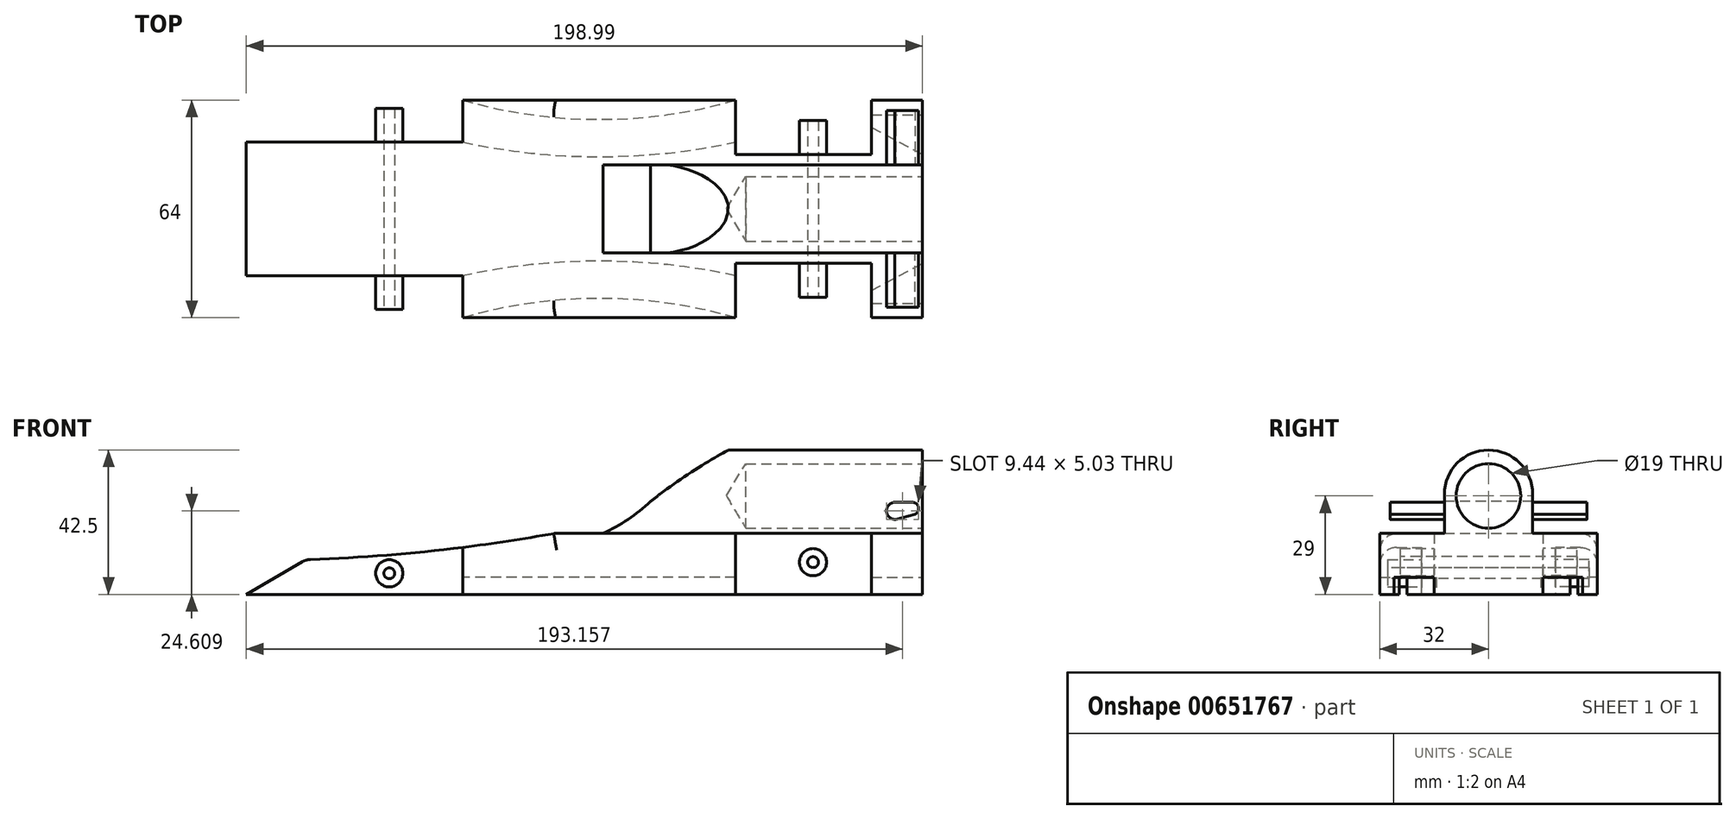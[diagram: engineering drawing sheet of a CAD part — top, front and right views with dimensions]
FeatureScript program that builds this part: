
annotation { "Feature Type Name" : "Feature", "Feature Type Description" : "" }
export const myFeature = defineFeature(function(context is Context, id is Id, definition is map)
    precondition{}
    {
        {
            var Q0;
            Q0=qCreatedBy(makeId("Front.planeOp"),FACE);
            var sketch = newSketch(context, id + "F0", { "sketchPlane" : qUnion([Q0])});
            skLineSegment(sketch, "E0", {"start": v(-86.8, 0) * mm, "end": v(113.2, 0) * mm});
            skLineSegment(sketch, "E1", {"start": v(113.2, 0) * mm, "end": v(113.2, 18) * mm});
            skLineSegment(sketch, "E2", {"start": v(-86.8, 0) * mm, "end": v(-86.8, 10) * mm});
            skLineSegment(sketch, "E3", {"start": v(113.2, 18) * mm, "end": v(5.13, 18) * mm});
            skArc(sketch, "E4", {"start": v(-86.8, 10) * mm, "mid": v(-40.65, 11.89) * mm, "end": v(5.13, 18) * mm});
            skSolve(sketch);
        }
        {
            var Q0;
            Q0=makeQuery(id+"F0.imprint","IMPRINT",FACE,{"disambiguationData":[TD([[makeQuery(id+"F0.imprint","IMPRINT",EDGE,{"derivedFrom":sQuery(id+"F0.wireOp",EDGE,"E0")}),1.0]])]});
            extrude(context, id + "F1", {"entities" : qUnion([Q0]), "oppositeDirection" : true, "depth" : 32 * mm, "offsetDistance" : 25 * mm});
        }
        {
            var Q0;
            Q0=makeQuery(id+"F1.opExtrude","SWEPT_FACE",FACE,{"disambiguationData":[OSD([sQuery(id+"F0.wireOp",EDGE,"E0")])]});
            var sketch = newSketch(context, id + "F2", { "sketchPlane" : qUnion([Q0])});
            skLineSegment(sketch, "E5", {"start": v(-22.02, -32) * mm, "end": v(-22.02, -19.65) * mm});
            skLineSegment(sketch, "E6", {"start": v(-22.02, -19.65) * mm, "end": v(-86.8, -19.65) * mm});
            skSolve(sketch);
        }
        {
            var Q0;
            Q0 = qSketchRegion(id + "F2", true);
            var Q1;
            {var subQ0=sQuery(id+"F2.wireOp",EDGE,"E5");Q1=makeQuery(id+"F2.imprint","IMPRINT",FACE,{"disambiguationData":[TD([[makeQuery(id+"F2.imprint","IMPRINT",EDGE,{"derivedFrom":subQ0}),1.0]])]});}
            extrude(context, id + "F3", {"entities" : qUnion([Q0, Q1]), "operationType" : NewBodyOperationType.REMOVE, "endBound" : BoundingType.THROUGH_ALL, "oppositeDirection" : true, "depth" : 25 * mm, "offsetDistance" : 25 * mm});
        }
        {
            var Q0;
            Q0=makeQuery(id+"F1.opExtrude","SWEPT_FACE",FACE,{"disambiguationData":[OSD([sQuery(id+"F0.wireOp",EDGE,"E0")])]});
            var sketch = newSketch(context, id + "F4", { "sketchPlane" : qUnion([Q0])});
            skLineSegment(sketch, "E7", {"start": v(113.2, -32) * mm, "end": v(98.2, -32) * mm, "construction": true});
            skLineSegment(sketch, "E8.bottom", {"start": v(98.2, -32) * mm, "end": v(58.2, -32) * mm});
            skLineSegment(sketch, "E8.top", {"start": v(98.2, -16) * mm, "end": v(58.2, -16) * mm});
            skLineSegment(sketch, "E8.left", {"start": v(98.2, -32) * mm, "end": v(98.2, -16) * mm});
            skLineSegment(sketch, "E8.right", {"start": v(58.2, -32) * mm, "end": v(58.2, -16) * mm});
            skSolve(sketch);
        }
        {
            var Q0;
            Q0=makeQuery(id+"F4.imprint","IMPRINT",FACE,{"disambiguationData":[TD([[makeQuery(id+"F4.imprint","IMPRINT",EDGE,{"derivedFrom":sQuery(id+"F4.wireOp",EDGE,"E8.bottom")}),1.0]])]});
            extrude(context, id + "F5", {"entities" : qUnion([Q0]), "operationType" : NewBodyOperationType.REMOVE, "endBound" : BoundingType.THROUGH_ALL, "oppositeDirection" : true, "depth" : 25 * mm, "offsetDistance" : 25 * mm});
        }
        {
            var Q0;
            Q0=makeQuery(id+"F1.opExtrude","SWEPT_FACE",FACE,{"disambiguationData":[OSD([sQuery(id+"F0.wireOp",EDGE,"E1")])]});
            var sketch = newSketch(context, id + "F6", { "sketchPlane" : qUnion([Q0])});
            skLineSegment(sketch, "E9", {"start": v(13, 18) * mm, "end": v(13, 29.5) * mm});
            skLineSegment(sketch, "E10", {"start": v(0, 18) * mm, "end": v(0, 42.5) * mm});
            skArc(sketch, "E11", {"start": v(13, 29.5) * mm, "mid": v(9.2, 38.7) * mm, "end": v(0, 42.5) * mm});
            skLineSegment(sketch, "E12", {"start": v(0, 18) * mm, "end": v(13, 18) * mm});
            skSolve(sketch);
        }
        {
            var Q0;
            {var subQ0=sQuery(id+"F6.wireOp",EDGE,"E9");Q0=makeQuery(id+"F6.imprint","IMPRINT",FACE,{"disambiguationData":[TD([[makeQuery(id+"F6.imprint","IMPRINT",EDGE,{"derivedFrom":subQ0}),1.0]])]});}
            extrude(context, id + "F7", {"entities" : qUnion([Q0]), "operationType" : NewBodyOperationType.ADD, "oppositeDirection" : true, "depth" : 80 * mm, "offsetDistance" : 25 * mm});
        }
        {
            var Q0;
            Q0=makeQuery(id+"F7.boolean.opBoolean","MERGE",FACE,{"derivedFrom":[makeQuery(id+"F1.opExtrude","CAP_FACE",FACE,{"disambiguationData":[OSD([sQuery(id+"F0.wireOp",EDGE,"E0"),sQuery(id+"F0.wireOp",EDGE,"E1"),sQuery(id+"F0.wireOp",EDGE,"E2"),sQuery(id+"F0.wireOp",EDGE,"E3"),sQuery(id+"F0.wireOp",EDGE,"E4")])],"isStart":true}),makeQuery(id+"F7.opExtrude","SWEPT_FACE",FACE,{"disambiguationData":[OSD([sQuery(id+"F6.wireOp",EDGE,"E10")])]})]});
            var sketch = newSketch(context, id + "F8", { "sketchPlane" : qUnion([Q0])});
            skArc(sketch, "E13", {"start": v(19.17, 18) * mm, "mid": v(33.82, 27.98) * mm, "end": v(44, 42.5) * mm});
            skSolve(sketch);
        }
        {
            var Q0;
            {var subQ0=sQuery(id+"F8.wireOp",EDGE,"E13");var subQ1=makeQuery(id+"F1.opExtrude","CAP_EDGE",EDGE,{"disambiguationData":[OSD([sQuery(id+"F0.wireOp",EDGE,"E3")])],"isStart":true});var subQ2=makeQuery(id+"F8.imprint","INTERSECT",VERTEX,{"derivedFrom":[subQ1,subQ0]});Q0=makeQuery(id+"F8.imprint","IMPRINT",FACE,{"disambiguationData":[TD([[makeQuery(id+"F8.imprint","IMPRINT",EDGE,{"disambiguationData":[TD([[subQ2,-1.0]])],"derivedFrom":subQ0}),-1.0]])]});}
            extrude(context, id + "F9", {"entities" : qUnion([Q0]), "operationType" : NewBodyOperationType.ADD, "oppositeDirection" : true, "depth" : 13 * mm, "offsetDistance" : 25 * mm});
        }
        {
            var Q0;
            {var subQ0=sQuery(id+"F6.wireOp",EDGE,"E10");var subQ1=sQuery(id+"F0.wireOp",EDGE,"E3");Q0=makeQuery(id+"F9.boolean.opBoolean","MERGE",FACE,{"derivedFrom":[makeQuery(id+"F7.boolean.opBoolean","MERGE",FACE,{"derivedFrom":[makeQuery(id+"F1.opExtrude","CAP_FACE",FACE,{"disambiguationData":[OSD([sQuery(id+"F0.wireOp",EDGE,"E0"),sQuery(id+"F0.wireOp",EDGE,"E1"),sQuery(id+"F0.wireOp",EDGE,"E2"),subQ1,sQuery(id+"F0.wireOp",EDGE,"E4")])],"isStart":true}),makeQuery(id+"F7.opExtrude","SWEPT_FACE",FACE,{"disambiguationData":[OSD([subQ0])]})]}),makeQuery(id+"F9.opExtrude","CAP_FACE",FACE,{"disambiguationData":[OSD([subQ1,subQ0,sQuery(id+"F8.wireOp",EDGE,"E13")])],"isStart":true})]});}
            var sketch = newSketch(context, id + "F10", { "sketchPlane" : qUnion([Q0])});
            skArc(sketch, "E14", {"start": v(56.09, 42.5) * mm, "mid": v(44.33, 35.42) * mm, "end": v(33.2, 27.39) * mm});
            skSolve(sketch);
        }
        {
            var Q0;
            {var subQ0=sQuery(id+"F10.wireOp",EDGE,"E14");Q0=makeQuery(id+"F10.imprint","IMPRINT",FACE,{"disambiguationData":[TD([[makeQuery(id+"F10.imprint","IMPRINT",EDGE,{"derivedFrom":subQ0}),-1.0]])]});}
            extrude(context, id + "F11", {"entities" : qUnion([Q0]), "operationType" : NewBodyOperationType.REMOVE, "endBound" : BoundingType.THROUGH_ALL, "oppositeDirection" : true, "depth" : 25 * mm, "offsetDistance" : 25 * mm});
        }
        {
            var Q0;
            {var subQ0=sQuery(id+"F0.wireOp",EDGE,"E0");var subQ1=sQuery(id+"F0.wireOp",EDGE,"E2");var subQ2=sQuery(id+"F0.wireOp",EDGE,"E4");Q0=makeQuery(id+"FZ9ZeYwKuadsPbT_1.boolean.opBoolean","SPLIT",FACE,{"disambiguationData":[TD([makeQuery(id+"F1.opExtrude","SWEPT_FACE",FACE,{"disambiguationData":[OSD([subQ1])]})])],"derivedFrom":makeQuery(id+"F1.opExtrude","CAP_FACE",FACE,{"disambiguationData":[OSD([subQ0,sQuery(id+"F0.wireOp",EDGE,"E1"),subQ1,sQuery(id+"F0.wireOp",EDGE,"E3"),subQ2])],"isStart":false})});}
            var sketch = newSketch(context, id + "F12", { "sketchPlane" : qUnion([Q0])});
            skSolve(sketch);
        }
        {
            var Q0;
            Q0=makeQuery(id+"F3.boolean.opBoolean","COPY",FACE,{"derivedFrom":makeQuery(id+"F3.opExtrude","SWEPT_FACE",FACE,{"disambiguationData":[OSD([sQuery(id+"F2.wireOp",EDGE,"E6")])]})});
            var sketch = newSketch(context, id + "F13", { "sketchPlane" : qUnion([Q0])});
            skCircle(sketch, "E15", {"center": v(43.7, 6.23) * mm, "radius": 4 * mm});
            skCircle(sketch, "E16", {"center": v(43.7, 6.23) * mm, "radius": 1.6 * mm});
            skSolve(sketch);
        }
        {
            var Q0;
            Q0=makeQuery(id+"F13.imprint","IMPRINT",FACE,{"disambiguationData":[TD([[makeQuery(id+"F13.imprint","IMPRINT",EDGE,{"derivedFrom":sQuery(id+"F13.wireOp",EDGE,"E15")}),1.0]])]});
            extrude(context, id + "F14", {"entities" : qUnion([Q0]), "operationType" : NewBodyOperationType.ADD, "depth" : 10 * mm, "offsetDistance" : 25 * mm});
        }
        {
            var Q0;
            Q0=makeQuery(id+"F14.boolean.opBoolean","SPLIT",FACE,{"disambiguationData":[TD([makeQuery(id+"F14.opExtrude","SWEPT_FACE",FACE,{"disambiguationData":[OSD([sQuery(id+"F13.wireOp",EDGE,"E16")])]})])],"derivedFrom":makeQuery(id+"F3.boolean.opBoolean","COPY",FACE,{"derivedFrom":makeQuery(id+"F3.opExtrude","SWEPT_FACE",FACE,{"disambiguationData":[OSD([sQuery(id+"F2.wireOp",EDGE,"E6")])]})})});
            extrude(context, id + "F15", {"entities" : qUnion([Q0]), "operationType" : NewBodyOperationType.REMOVE, "endBound" : BoundingType.THROUGH_ALL, "oppositeDirection" : true, "depth" : 25 * mm, "offsetDistance" : 25 * mm});
        }
        {
            var Q0;
            Q0=makeQuery(id+"F5.boolean.opBoolean","COPY",FACE,{"derivedFrom":makeQuery(id+"F5.opExtrude","SWEPT_FACE",FACE,{"disambiguationData":[OSD([sQuery(id+"F4.wireOp",EDGE,"E8.top")])]})});
            var sketch = newSketch(context, id + "F16", { "sketchPlane" : qUnion([Q0])});
            skCircle(sketch, "E17", {"center": v(-81, 9.5) * mm, "radius": 4 * mm});
            skCircle(sketch, "E18", {"center": v(-81, 9.5) * mm, "radius": 1.6 * mm});
            skSolve(sketch);
        }
        {
            var Q0;
            Q0=makeQuery(id+"F16.imprint","IMPRINT",FACE,{"disambiguationData":[TD([[makeQuery(id+"F16.imprint","IMPRINT",EDGE,{"derivedFrom":sQuery(id+"F16.wireOp",EDGE,"E17")}),1.0]])]});
            extrude(context, id + "F17", {"entities" : qUnion([Q0]), "operationType" : NewBodyOperationType.ADD, "depth" : 10 * mm, "offsetDistance" : 25 * mm});
        }
        {
            var Q0;
            Q0=makeQuery(id+"F17.boolean.opBoolean","SPLIT",FACE,{"disambiguationData":[TD([makeQuery(id+"F17.opExtrude","SWEPT_FACE",FACE,{"disambiguationData":[OSD([sQuery(id+"F16.wireOp",EDGE,"E18")])]})])],"derivedFrom":makeQuery(id+"F5.boolean.opBoolean","COPY",FACE,{"derivedFrom":makeQuery(id+"F5.opExtrude","SWEPT_FACE",FACE,{"disambiguationData":[OSD([sQuery(id+"F4.wireOp",EDGE,"E8.top")])]})})});
            extrude(context, id + "F18", {"entities" : qUnion([Q0]), "operationType" : NewBodyOperationType.REMOVE, "endBound" : BoundingType.THROUGH_ALL, "oppositeDirection" : true, "depth" : 25 * mm, "offsetDistance" : 25 * mm});
        }
        {
            var Q0;
            {var subQ0=sQuery(id+"F6.wireOp",EDGE,"E9");Q0=makeQuery(id+"F0brN90eAgxFyRM_1.boolean.opBoolean","MERGE",FACE,{"derivedFrom":[makeQuery(id+"F7.boolean.opBoolean","MERGE",FACE,{"derivedFrom":[makeQuery(id+"F1.opExtrude","SWEPT_FACE",FACE,{"disambiguationData":[OSD([sQuery(id+"F0.wireOp",EDGE,"E1")])]}),makeQuery(id+"F7.opExtrude","CAP_FACE",FACE,{"disambiguationData":[OSD([subQ0,sQuery(id+"F6.wireOp",EDGE,"E10"),sQuery(id+"F6.wireOp",EDGE,"E11"),sQuery(id+"F6.wireOp",EDGE,"E12")])],"isStart":true})]}),makeQuery(id+"F0brN90eAgxFyRM_1.opExtrude","SWEPT_FACE",FACE,{"disambiguationData":[OSD([subQ0])]})]});}
            var sketch = newSketch(context, id + "F19", { "sketchPlane" : qUnion([Q0])});
            skPoint(sketch, "E19", {"position": v(0, 29) * mm});
            skSolve(sketch);
        }
        {
            var Q0;
            Q0=sQuery(id+"F19.wireOp",VERTEX,"E19");
            var Q1;
            Q1=makeQuery(id+"F1.opExtrude","SWEPT_BODY",BODY,{"disambiguationData":[OSD([sQuery(id+"F0.wireOp",EDGE,"E0"),sQuery(id+"F0.wireOp",EDGE,"E1"),sQuery(id+"F0.wireOp",EDGE,"E2"),sQuery(id+"F0.wireOp",EDGE,"E3"),sQuery(id+"F0.wireOp",EDGE,"E4")])]});
            hole(context, id + "F20", {"style" : HoleStyle.SIMPLE, "endStyle" : HoleEndStyle.BLIND, "holeDiameter" : 19 * mm, "majorDiameter" : 5 * mm, "holeDepth" : 52 * mm, "isTappedThrough" : true, "tappedDepth" : 12 * mm, "tapClearance" : 3, "locations" : qUnion([Q0]), "scope" : qUnion([Q1])});
        }
        {
            var Q0;
            Q0=makeQuery(id+"F7.opExtrude","SWEPT_FACE",FACE,{"disambiguationData":[OSD([sQuery(id+"F6.wireOp",EDGE,"E9")])]});
            var sketch = newSketch(context, id + "F21", { "sketchPlane" : qUnion([Q0])});
            skArc(sketch, "E20", {"start": v(-105.34, 22.1) * mm, "mid": v(-102.65, 24.47) * mm, "end": v(-105.05, 27.12) * mm});
            skLineSegment(sketch, "E21", {"start": v(-105.34, 22.1) * mm, "end": v(-111.07, 23.58) * mm});
            skLineSegment(sketch, "E22", {"start": v(-105.05, 27.12) * mm, "end": v(-110.22, 27.12) * mm});
            skArc(sketch, "E23", {"start": v(-110.22, 27.12) * mm, "mid": v(-112.04, 25.69) * mm, "end": v(-111.07, 23.58) * mm});
            skSolve(sketch);
        }
        {
            var Q0;
            {var subQ0=sQuery(id+"F0.wireOp",EDGE,"E4");var subQ1=sQuery(id+"F0.wireOp",EDGE,"E3");Q0=makeQuery(id+"F5.boolean.opBoolean","SPLIT",EDGE,{"disambiguationData":[TD([makeQuery(id+"F1.opExtrude","SWEPT_FACE",FACE,{"disambiguationData":[OSD([subQ0])]})])],"derivedFrom":makeQuery(id+"F1.opExtrude","CAP_EDGE",EDGE,{"disambiguationData":[OSD([subQ1])],"isStart":false})});}
            var Q1;
            Q1=makeQuery(id+"F1.opExtrude","CAP_EDGE",EDGE,{"disambiguationData":[OSD([sQuery(id+"F0.wireOp",EDGE,"E4")])],"isStart":false});
            fillet(context, id + "F22", {"entities" : qUnion([Q0, Q1]), "radius" : 5 * mm, "tangentPropagation" : true, "allowEdgeOverflow" : false});
        }
        {
            var Q0;
            Q0=makeQuery(id+"F1.opExtrude","SWEPT_FACE",FACE,{"disambiguationData":[OSD([sQuery(id+"F0.wireOp",EDGE,"E0")])]});
            var sketch = newSketch(context, id + "F23", { "sketchPlane" : qUnion([Q0])});
            skArc(sketch, "E24", {"start": v(58.2, -32) * mm, "mid": v(18.1, -26.34) * mm, "end": v(-22.02, -32) * mm});
            skArc(sketch, "E25", {"start": v(58.2, -19.65) * mm, "mid": v(18.1, -15.36) * mm, "end": v(-22.02, -19.65) * mm});
            skSolve(sketch);
        }
        {
            var Q0;
            {var subQ0=sQuery(id+"F23.wireOp",EDGE,"E24");Q0=makeQuery(id+"F23.imprint","IMPRINT",FACE,{"disambiguationData":[TD([[makeQuery(id+"F23.imprint","IMPRINT",EDGE,{"derivedFrom":subQ0}),-1.0]])]});}
            extrude(context, id + "F24", {"entities" : qUnion([Q0]), "operationType" : NewBodyOperationType.REMOVE, "oppositeDirection" : true, "depth" : 5 * mm, "offsetDistance" : 25 * mm});
        }
        {
            var Q0;
            {var subQ1=sQuery(id+"F0.wireOp",EDGE,"E1");var subQ2=makeQuery(id+"F1.opExtrude","SWEPT_FACE",FACE,{"disambiguationData":[OSD([subQ1])]});var subQ3=makeQuery(id+"F5.boolean.opBoolean","COPY",FACE,{"derivedFrom":makeQuery(id+"F5.opExtrude","SWEPT_FACE",FACE,{"disambiguationData":[OSD([sQuery(id+"F4.wireOp",EDGE,"E8.top")])]})});var subQ8=sQuery(id+"F0.wireOp",EDGE,"E0");Q0=makeQuery(id+"F24.boolean.opBoolean","SPLIT",FACE,{"disambiguationData":[TD([subQ3])],"derivedFrom":makeQuery(id+"FajyCnxoudD1aa0_1.boolean.opBoolean","SPLIT",FACE,{"disambiguationData":[TD([subQ2])],"derivedFrom":makeQuery(id+"F1.opExtrude","SWEPT_FACE",FACE,{"disambiguationData":[OSD([subQ8])]})})});}
            var sketch = newSketch(context, id + "F25", { "sketchPlane" : qUnion([Q0])});
            skLineSegment(sketch, "E26", {"start": v(98.2, -24) * mm, "end": v(113.2, -16) * mm});
            skLineSegment(sketch, "E27", {"start": v(98.2, -27.75) * mm, "end": v(113.2, -27.75) * mm});
            skSolve(sketch);
        }
        {
            var Q0;
            {var subQ0=sQuery(id+"F25.wireOp",EDGE,"E26");Q0=makeQuery(id+"F25.imprint","IMPRINT",FACE,{"disambiguationData":[TD([[makeQuery(id+"F25.imprint","IMPRINT",EDGE,{"derivedFrom":subQ0}),-1.0]])]});}
            extrude(context, id + "F26", {"entities" : qUnion([Q0]), "operationType" : NewBodyOperationType.REMOVE, "oppositeDirection" : true, "depth" : 5 * mm, "offsetDistance" : 25 * mm});
        }
        {
            var Q0;
            Q0=makeQuery(id+"F21.imprint","IMPRINT",FACE,{"disambiguationData":[TD([[makeQuery(id+"F21.imprint","IMPRINT",EDGE,{"derivedFrom":sQuery(id+"F21.wireOp",EDGE,"E20")}),1.0]])]});
            extrude(context, id + "F27", {"entities" : qUnion([Q0]), "operationType" : NewBodyOperationType.ADD, "depth" : 16 * mm, "offsetDistance" : 25 * mm});
        }
        {
            var Q0;
            Q0=makeQuery(id+"F1.opExtrude","SWEPT_BODY",BODY,{"disambiguationData":[OSD([sQuery(id+"F0.wireOp",EDGE,"E0"),sQuery(id+"F0.wireOp",EDGE,"E1"),sQuery(id+"F0.wireOp",EDGE,"E2"),sQuery(id+"F0.wireOp",EDGE,"E3"),sQuery(id+"F0.wireOp",EDGE,"E4")])]});
            var Q1;
            Q1=makeQuery(id+"FBDryquV3LORY7v_1.boolean.opBoolean","MERGE",FACE,{"derivedFrom":[makeQuery(id+"F7.boolean.opBoolean","MERGE",FACE,{"derivedFrom":[makeQuery(id+"F1.opExtrude","CAP_FACE",FACE,{"disambiguationData":[OSD([sQuery(id+"F0.wireOp",EDGE,"E0"),sQuery(id+"F0.wireOp",EDGE,"E1"),sQuery(id+"F0.wireOp",EDGE,"E2"),sQuery(id+"F0.wireOp",EDGE,"E3"),sQuery(id+"F0.wireOp",EDGE,"E4")])],"isStart":true}),makeQuery(id+"F7.opExtrude","SWEPT_FACE",FACE,{"disambiguationData":[OSD([sQuery(id+"F6.wireOp",EDGE,"E10")])]})]}),makeQuery(id+"FBDryquV3LORY7v_1.opExtrude","SWEPT_FACE",FACE,{"disambiguationData":[OSD([sQuery(id+"FW7ZlxmGJCiysjx_1.wireOp",EDGE,"aqjsSCQp-a6w5-974F-Gjd7-LcsiUKuWwMjG")])]})]});
            mirror(context, id + "F28", {"operationType" : NewBodyOperationType.ADD, "entities" : qUnion([Q0]), "mirrorPlane" : qUnion([Q1])});
        }
        {
            var Q0;
            Q0=makeQuery(id+"Fd1yMICXianF2rR_1.boolean.opBoolean","COPY",EDGE,{"derivedFrom":makeQuery(id+"Fd1yMICXianF2rR_1.opExtrude","SWEPT_EDGE",EDGE,{"disambiguationData":[OSD([sQuery(id+"FEK0vznBMnfqPsM_1.wireOp",EDGE,"FlV3PyBM-Jq2D-pZNL-DW5d-tzeu0OckHNhe"),sQuery(id+"FLLcgn1Dg8ij81G_1.wireOp",EDGE,"QmvrM2vS-eiQj-ILNC-KOxQ-fQvgeKDZ8A3c")])]})});
            var Q1;
            Q1=makeQuery(id+"Fd1yMICXianF2rR_1.boolean.opBoolean","COPY",EDGE,{"derivedFrom":makeQuery(id+"Fd1yMICXianF2rR_1.opExtrude","SWEPT_EDGE",EDGE,{"disambiguationData":[OSD([sQuery(id+"F12.wireOp",EDGE,"j4vxX2xc-Jvk5-80Qv-zy9u-17DE060Fgxmz"),sQuery(id+"FLLcgn1Dg8ij81G_1.wireOp",EDGE,"QmvrM2vS-eiQj-ILNC-KOxQ-fQvgeKDZ8A3c")])]})});
            var Q2;
            Q2=makeQuery(id+"F1.opExtrude","SWEPT_EDGE",EDGE,{"disambiguationData":[OSD([sQuery(id+"F0.wireOp",EDGE,"E3"),sQuery(id+"F0.wireOp",EDGE,"E4")])]});
            var Q3;
            Q3=makeQuery(id+"F7.opExtrude","CAP_EDGE",EDGE,{"disambiguationData":[OSD([sQuery(id+"F6.wireOp",EDGE,"E9")])],"isStart":false});
            fillet(context, id + "F29", {"entities" : qUnion([Q0, Q1, Q2, Q3]), "radius" : 5 * mm, "tangentPropagation" : true, "allowEdgeOverflow" : false});
        }
        {
            var Q0;
            {var subQ0=makeQuery(id+"F1.opExtrude","SWEPT_EDGE",EDGE,{"disambiguationData":[OSD([sQuery(id+"F0.wireOp",EDGE,"E2"),sQuery(id+"F0.wireOp",EDGE,"E4")])]});Q0=makeQuery(id+"FD6PCLpWwn2yxJw_1.boolean.opBoolean","MERGE",EDGE,{"derivedFrom":[subQ0,makeQuery(id+"FD6PCLpWwn2yxJw_1.opPattern","COPY",EDGE,{"derivedFrom":subQ0,"instanceName":"1"})]});}
            chamfer(context, id + "F30", {"entities" : qUnion([Q0]), "chamferType" : ChamferType.OFFSET_ANGLE, "width" : 19 * mm, "oppositeDirection" : false, "angle" : 30 * degree});
        }
        {
            var Q0;
            {var subQ0=sQuery(id+"F0.wireOp",EDGE,"E4");var subQ1=makeQuery(id+"F1.opExtrude","SWEPT_FACE",FACE,{"disambiguationData":[OSD([subQ0])]});var subQ2=makeQuery(id+"F1.opExtrude","SWEPT_EDGE",EDGE,{"disambiguationData":[OSD([sQuery(id+"F0.wireOp",EDGE,"E2"),subQ0])]});Q0=makeQuery(id+"F30.opChamfer","BLEND_EDGE",EDGE,{"blendedFrom":[makeQuery(id+"F28.boolean.opBoolean","MERGE",EDGE,{"derivedFrom":[subQ2,makeQuery(id+"F28.opPattern","COPY",EDGE,{"derivedFrom":subQ2,"instanceName":"1"})]}),makeQuery(id+"F28.boolean.opBoolean","MERGE",FACE,{"derivedFrom":[subQ1,makeQuery(id+"F28.opPattern","COPY",FACE,{"derivedFrom":subQ1,"instanceName":"1"})]})],"blendedInto":[makeQuery(id+"F28.boolean.opBoolean","MERGE",FACE,{"derivedFrom":[subQ1,makeQuery(id+"F28.opPattern","COPY",FACE,{"derivedFrom":subQ1,"instanceName":"1"})]})]});}
            fillet(context, id + "F31", {"entities" : qUnion([Q0]), "radius" : 5 * mm, "tangentPropagation" : true, "allowEdgeOverflow" : false});
        }
    });
